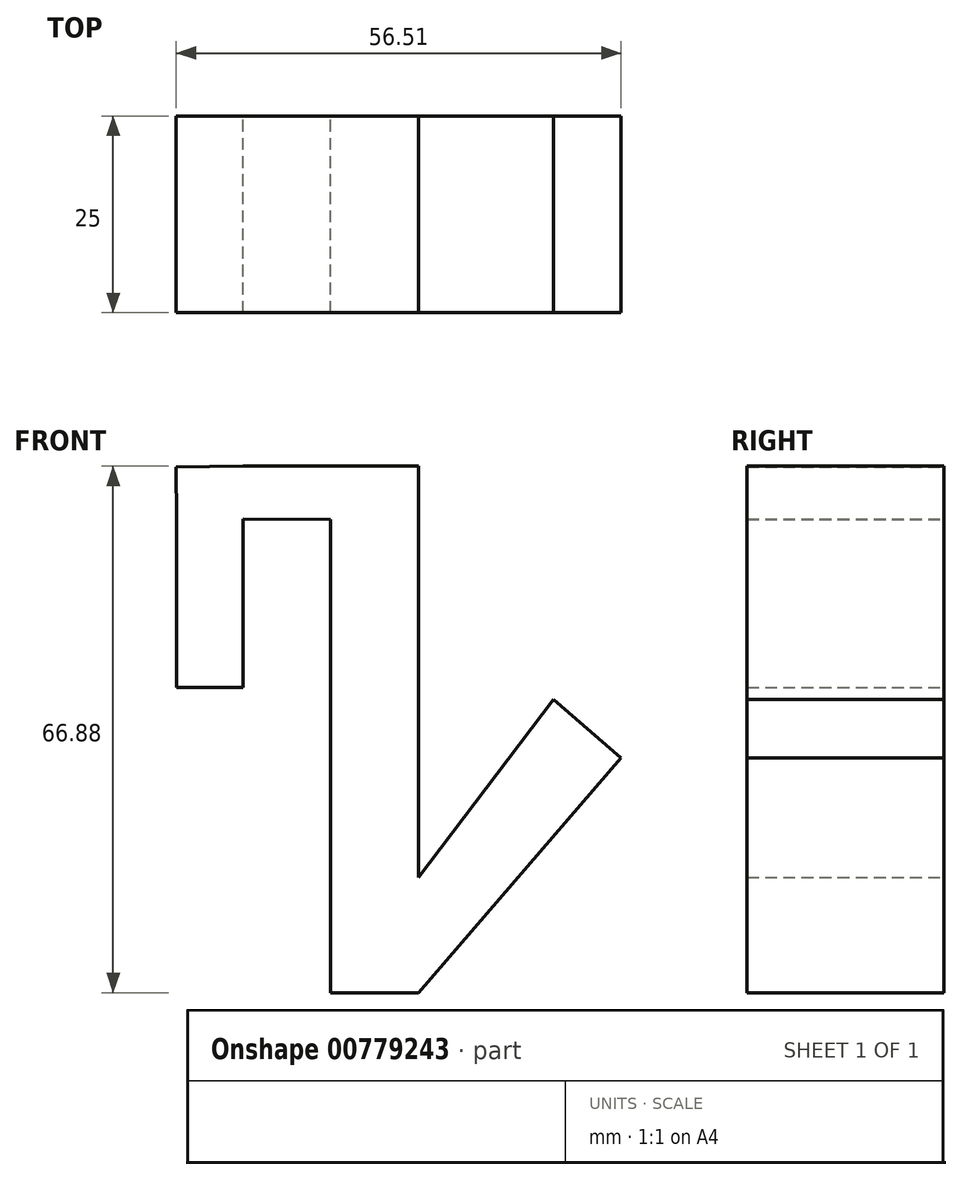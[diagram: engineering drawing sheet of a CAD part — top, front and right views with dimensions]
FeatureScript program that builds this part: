
annotation { "Feature Type Name" : "Feature", "Feature Type Description" : "" }
export const myFeature = defineFeature(function(context is Context, id is Id, definition is map)
    precondition{}
    {
        {
            var Q0;
            Q0=qCreatedBy(makeId("Front.planeOp"),FACE);
            var sketch = newSketch(context, id + "F0", { "sketchPlane" : qUnion([Q0])});
            skLineSegment(sketch, "E0", {"start": v(-32.08, 38.96) * mm, "end": v(-32.08, 17.66) * mm});
            skLineSegment(sketch, "E1", {"start": v(-32.08, 17.66) * mm, "end": v(-23.67, 17.66) * mm});
            skLineSegment(sketch, "E2", {"start": v(-23.67, 17.66) * mm, "end": v(-23.67, 39.04) * mm});
            skLineSegment(sketch, "E3", {"start": v(-23.67, 39.04) * mm, "end": v(-32.08, 38.96) * mm});
            skLineSegment(sketch, "E4", {"start": v(-32.08, 38.96) * mm, "end": v(-32.14, 45.66) * mm});
            skLineSegment(sketch, "E5", {"start": v(-32.14, 45.66) * mm, "end": v(-23.67, 45.74) * mm});
            skLineSegment(sketch, "E6", {"start": v(-23.67, 45.74) * mm, "end": v(-1.37, 45.74) * mm});
            skLineSegment(sketch, "E7", {"start": v(-1.37, 45.74) * mm, "end": v(-1.37, 38.96) * mm});
            skLineSegment(sketch, "E8", {"start": v(-1.37, 38.96) * mm, "end": v(-23.67, 39.04) * mm});
            skLineSegment(sketch, "E9", {"start": v(-12.52, 45.74) * mm, "end": v(-12.52, -21.14) * mm});
            skLineSegment(sketch, "E10", {"start": v(-12.52, -21.14) * mm, "end": v(-1.37, -21.14) * mm});
            skLineSegment(sketch, "E11", {"start": v(-1.37, -21.14) * mm, "end": v(-1.37, 45.74) * mm});
            skPoint(sketch, "E12", {"position": v(-23.67, 28.35) * mm});
            skPoint(sketch, "E13", {"position": v(-12.52, 28.35) * mm});
            skLineSegment(sketch, "E14", {"start": v(-1.37, -21.14) * mm, "end": v(24.37, 8.67) * mm});
            skLineSegment(sketch, "E15", {"start": v(24.37, 8.67) * mm, "end": v(15.78, 16.09) * mm});
            skLineSegment(sketch, "E16", {"start": v(15.78, 16.09) * mm, "end": v(-12.52, -21.14) * mm});
            skLineSegment(sketch, "E17", {"start": v(-12.52, 45.74) * mm, "end": v(-1.37, 38.96) * mm});
            skSolve(sketch);
        }
        {
            var Q0;
            Q0 = qSketchRegion(id + "F0", true);
            extrude(context, id + "F1", {"entities" : qUnion([Q0]), "depth" : 25 * mm, "offsetDistance" : 25 * mm});
        }
    });
